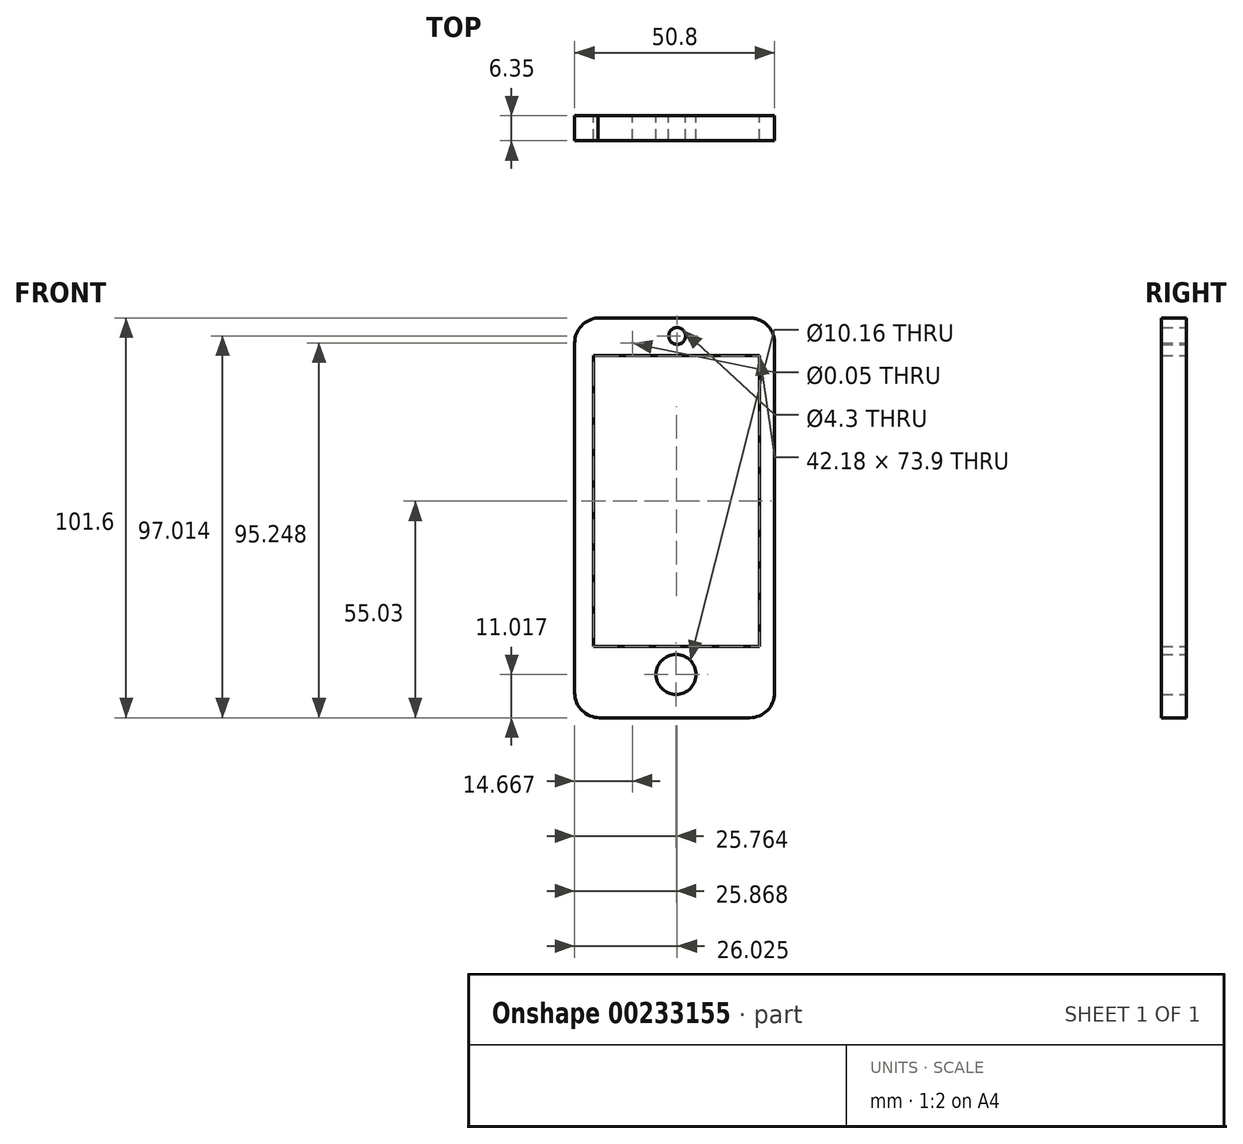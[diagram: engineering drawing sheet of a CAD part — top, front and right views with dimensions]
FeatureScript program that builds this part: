
annotation { "Feature Type Name" : "Feature", "Feature Type Description" : "" }
export const myFeature = defineFeature(function(context is Context, id is Id, definition is map)
    precondition{}
    {
        {
            var Q0;
            Q0=qCreatedBy(makeId("Front.planeOp"),FACE);
            var sketch = newSketch(context, id + "F0", { "sketchPlane" : qUnion([Q0])});
            skLineSegment(sketch, "E0", {"start": v(-61.32, 56.34) * mm, "end": v(-61.32, -32.56) * mm});
            skLineSegment(sketch, "E1", {"start": v(-54.97, -38.91) * mm, "end": v(-16.87, -38.91) * mm});
            skArc(sketch, "E2.filletArc", {"start": v(-55.4, 62.67) * mm, "mid": v(-59.61, 60.67) * mm, "end": v(-61.32, 56.34) * mm});
            skArc(sketch, "E3.filletArc", {"start": v(-61.32, -32.56) * mm, "mid": v(-59.46, -37.05) * mm, "end": v(-54.97, -38.91) * mm});
            skLineSegment(sketch, "E4", {"start": v(-10.52, -32.56) * mm, "end": v(-10.52, 56.34) * mm});
            skArc(sketch, "E5.filletArc", {"start": v(-10.52, 56.34) * mm, "mid": v(-12.38, 60.83) * mm, "end": v(-16.87, 62.69) * mm});
            skArc(sketch, "E6.filletArc", {"start": v(-16.87, -38.91) * mm, "mid": v(-12.38, -37.05) * mm, "end": v(-10.52, -32.56) * mm});
            skCircle(sketch, "E7", {"center": v(-35.56, -27.9) * mm, "radius": 5.08 * mm});
            skLineSegment(sketch, "E8", {"start": v(-56.54, 53.07) * mm, "end": v(-14.36, 53.07) * mm});
            skLineSegment(sketch, "E9", {"start": v(-56.54, 53.07) * mm, "end": v(-56.54, -20.83) * mm});
            skLineSegment(sketch, "E10", {"start": v(-56.54, -20.83) * mm, "end": v(-14.36, -20.83) * mm});
            skLineSegment(sketch, "E11", {"start": v(-14.36, 53.07) * mm, "end": v(-14.36, -20.83) * mm});
            skCircle(sketch, "E12", {"center": v(-46.65, 56.34) * mm, "radius": 0.03 * mm});
            skCircle(sketch, "E13", {"center": v(-35.3, 58.1) * mm, "radius": 2.15 * mm});
            skPoint(sketch, "E13.centerSnap0", {"position": v(-35.3, 62.69) * mm});
            skLineSegment(sketch, "E14", {"start": v(-55.4, 62.67) * mm, "end": v(-16.87, 62.69) * mm});
            skSolve(sketch);
        }
        {
            var Q0;
            Q0 = qSketchRegion(id + "F0", true);
            extrude(context, id + "F1", {"entities" : qUnion([Q0]), "depth" : 6.35 * mm});
        }
    });
